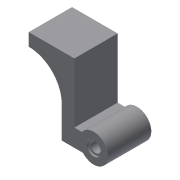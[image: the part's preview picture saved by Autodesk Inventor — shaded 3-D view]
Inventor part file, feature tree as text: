
AUTODESK INVENTOR PART (.ipt)
format: ipt  version: 2015 (Build 190159000, 159)  size: 157,696 bytes
history: native  units: in
note: dims shown in document units (in); Inventor stores cm internally (conversion verified against a paired STEP export)
features: extrude x6, sketch x6, mirror x3, projected_geometry x2, fillet x1, reference x1
ambient origin geometry x8: Origin, YZ Plane, XZ Plane, XY Plane, X Axis, Y Axis, Z Axis, Center Point
bodies: Solid1 (feature_tree)
feature tree (19):
  extrude  "Extrusion1"  Depth=0.9375in TaperAngle=0.0deg
  extrude  "Extrusion2"  Depth=0.4882in TaperAngle=0.0deg
  mirror  "Mirror1"
  extrude  "Extrusion3"  Depth=0.0591in TaperAngle=0.0deg
  extrude  "Extrusion4"  Depth=0.3831in
  mirror  "Mirror2"
  extrude  "Extrusion5"  Depth=1.0in
  fillet  "Fillet3"  Radius=1.0in
  extrude  "Extrusion6"  [1 undecoded]
  mirror  "Mirror4"
  sketch  "Sketch1"  dims[d0=0.375in d1=0.0in d2=0.9375in d3=0.0in]
  reference  "Reference1"
  sketch  "Sketch2"  dims[d4=0.3125in d5=0.4882in d6=0.0in]
  sketch  "Sketch3"  dims[d7=0.4331in d8=0.0591in d9=0.0in]
  sketch  "Sketch4"  dims[d11=2.3455in d12=0.3831in]
  sketch  "Sketch7"  dims[d13=1.0in d14=0.0in d16=1.0in d17=1.0in d18=0.0in]
  projected_geometry  "Projected Loop1"
  sketch  "Sketch9"
  projected_geometry  "Projected Loop2"
note: 1 required parameter value undecoded (feature->parameter linkage not recoverable at this tier; creation-order binding heuristic only, values carry confidence <= 0.55)
